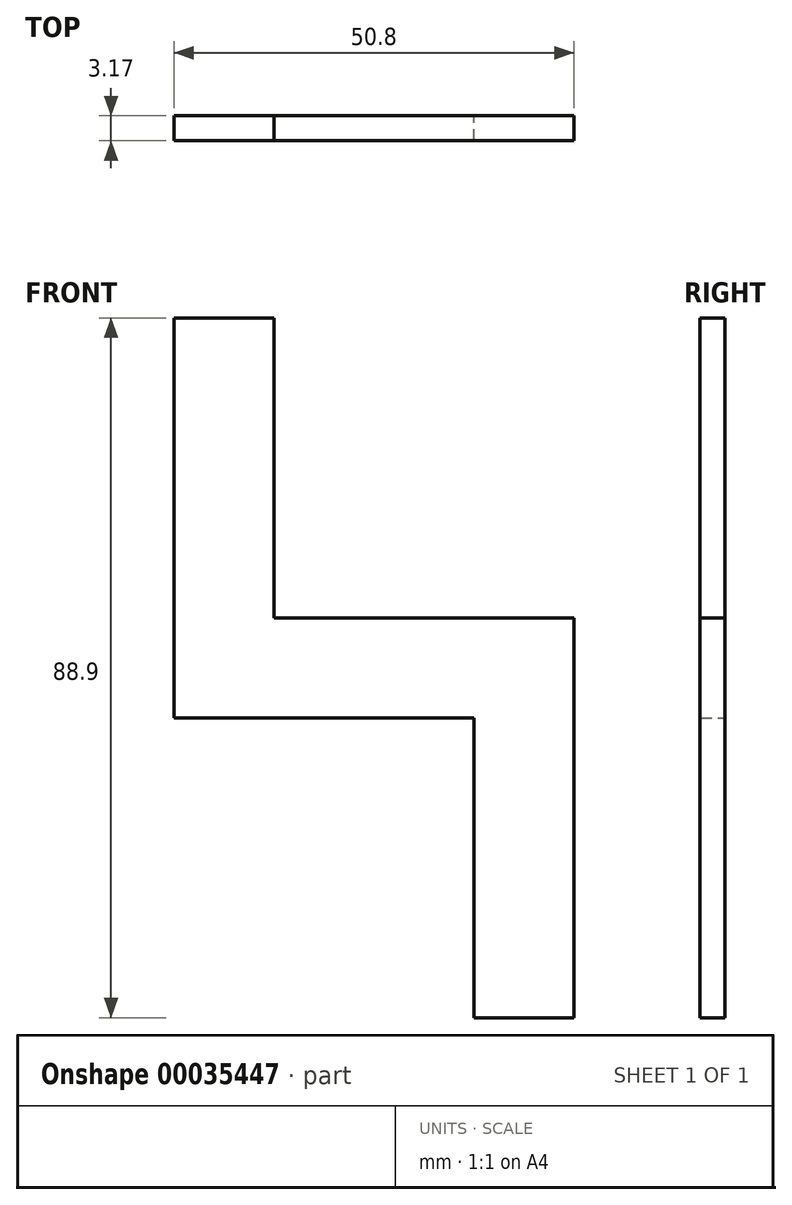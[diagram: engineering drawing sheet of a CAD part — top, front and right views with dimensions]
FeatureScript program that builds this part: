
annotation { "Feature Type Name" : "Feature", "Feature Type Description" : "" }
export const myFeature = defineFeature(function(context is Context, id is Id, definition is map)
    precondition{}
    {
        {
            var Q0;
            Q0=qCreatedBy(makeId("Front.planeOp"),FACE);
            var sketch = newSketch(context, id + "F0", { "sketchPlane" : qUnion([Q0])});
            skLineSegment(sketch, "E0.bottom", {"start": v(-50.8, 50.8) * mm, "end": v(-38.1, 50.8) * mm});
            skLineSegment(sketch, "E0.top", {"start": v(-50.8, 0) * mm, "end": v(-38.1, 0) * mm});
            skLineSegment(sketch, "E0.left", {"start": v(-50.8, 50.8) * mm, "end": v(-50.8, 0) * mm});
            skLineSegment(sketch, "E0.right", {"start": v(-38.1, 50.8) * mm, "end": v(-38.1, 0) * mm});
            skLineSegment(sketch, "E1.bottom", {"start": v(-50.8, 12.7) * mm, "end": v(0, 12.7) * mm});
            skLineSegment(sketch, "E1.top", {"start": v(-50.8, 0) * mm, "end": v(0, 0) * mm});
            skLineSegment(sketch, "E1.left", {"start": v(-50.8, 12.7) * mm, "end": v(-50.8, 0) * mm});
            skLineSegment(sketch, "E1.right", {"start": v(0, 12.7) * mm, "end": v(0, 0) * mm});
            skLineSegment(sketch, "E2.bottom", {"start": v(0, 12.7) * mm, "end": v(-12.7, 12.7) * mm});
            skLineSegment(sketch, "E2.top", {"start": v(0, -38.1) * mm, "end": v(-12.7, -38.1) * mm});
            skLineSegment(sketch, "E2.left", {"start": v(0, 12.7) * mm, "end": v(0, -38.1) * mm});
            skLineSegment(sketch, "E2.right", {"start": v(-12.7, 12.7) * mm, "end": v(-12.7, -38.1) * mm});
            skSolve(sketch);
        }
        {
            var Q0;
            Q0 = qSketchRegion(id + "F0", true);
            extrude(context, id + "F1", {"entities" : qUnion([Q0]), "depth" : 3.17 * mm});
        }
    });
